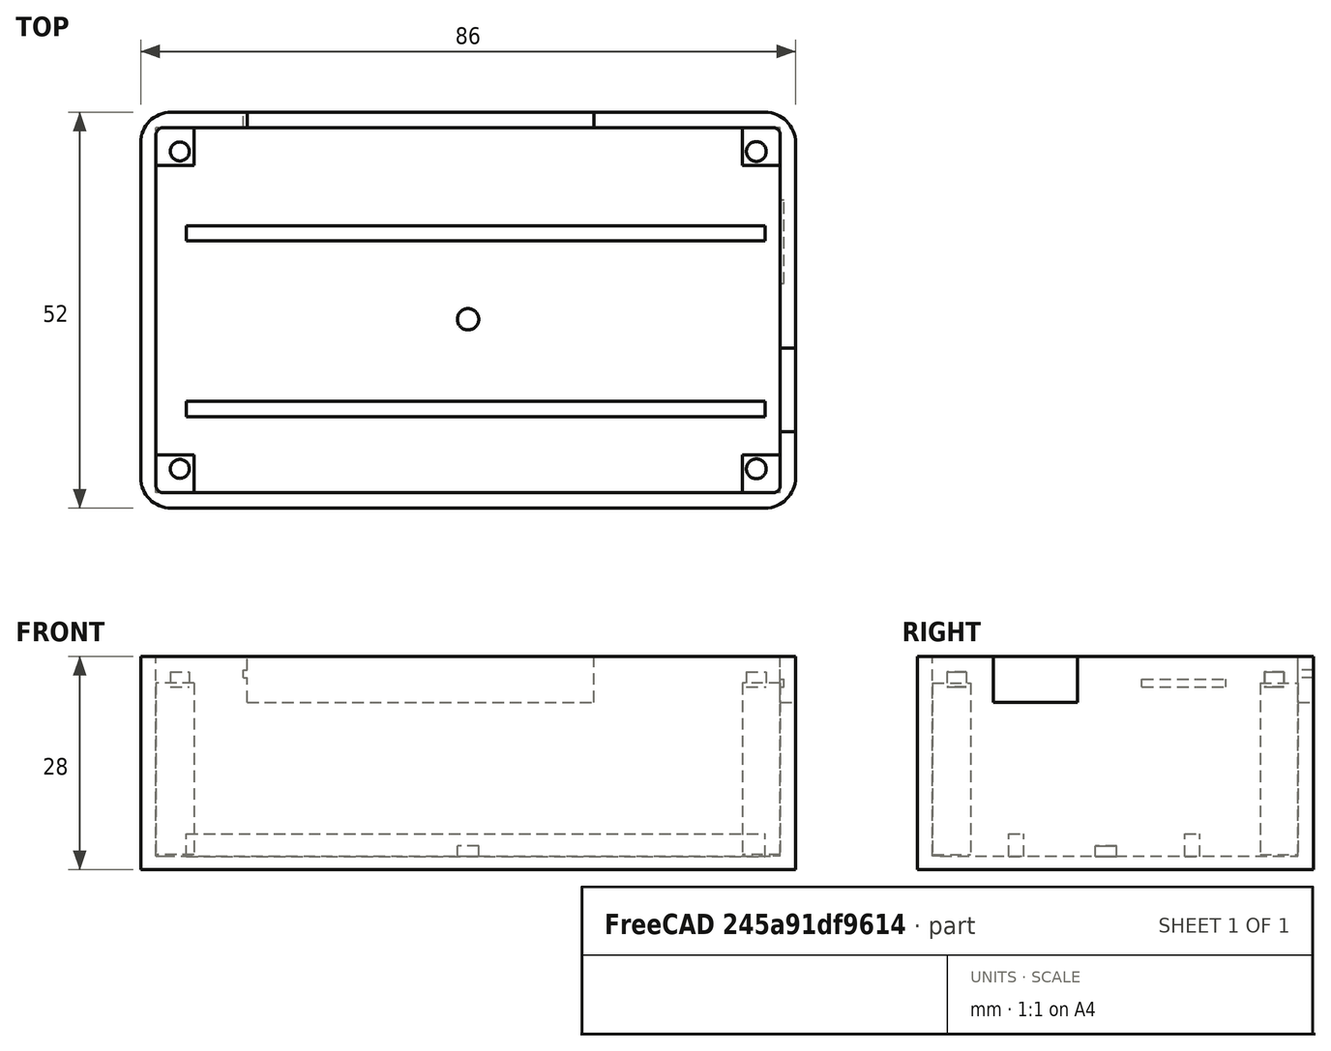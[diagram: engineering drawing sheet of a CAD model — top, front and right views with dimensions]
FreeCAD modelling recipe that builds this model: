
FCSTD DOCUMENT  (FreeCAD 0.18R4 (GitTag))
Label: T5s Case V6
License: All rights reserved
LicenseURL: http://en.wikipedia.org/wiki/All_rights_reserved
objects: Part::Box×12, Part::Cylinder×5, Part::Cut×4, App::DocumentObjectGroup×2, Part::Fillet×2, Part::Fuse×1
note: 24 computed .brp shape members not serialized (recipe doc carries the construction recipe); baked Part::Feature solids carry a one-line shape summary decoded from their .brp

FEATURE [Part::Box] Box004  label="Column1"
  AttacherType = Attacher::AttachEngine3D
  Height = 22.5
  Length = 5
  Placement = pos=(-36,19,9.5) rot=(0,1,0;3.14159rad)
  Width = 5
FEATURE [Part::Cylinder] Cylinder  label="Column Cylinder 1"
  Angle = 360
  AttacherType = Attacher::AttachEngine3D
  Height = 2
  Placement = pos=(-37.85,20.85,11) rot=(0,1,0;3.14159rad)
  Radius = 1.25
FEATURE [Part::Box] Box006  label="Column3"
  AttacherType = Attacher::AttachEngine3D
  Height = 22.5
  Length = 5
  Placement = pos=(-36,-24,9.5) rot=(0,1,0;3.14159rad)
  Width = 5
FEATURE [Part::Box] Box005  label="Column2"
  AttacherType = Attacher::AttachEngine3D
  Height = 22.5
  Length = 5
  Placement = pos=(41,19,9.5) rot=(0,1,0;3.14159rad)
  Width = 5
FEATURE [Part::Cylinder] Cylinder001  label="Column Cylinder 3"
  Angle = 360
  AttacherType = Attacher::AttachEngine3D
  Height = 2
  Placement = pos=(-37.85,-20.85,11) rot=(0,1,0;3.14159rad)
  Radius = 1.25
FEATURE [Part::Box] Box007  label="Column4"
  AttacherType = Attacher::AttachEngine3D
  Height = 22.5
  Length = 5
  Placement = pos=(41,-24,9.5) rot=(0,1,0;3.14159rad)
  Width = 5
FEATURE [Part::Cylinder] Cylinder002  label="Column Cylinder 2"
  Angle = 360
  AttacherType = Attacher::AttachEngine3D
  Height = 2
  Placement = pos=(37.85,20.85,11) rot=(0,1,0;3.14159rad)
  Radius = 1.3
FEATURE [Part::Cylinder] Cylinder003  label="Column Cylinder 4"
  Angle = 360
  AttacherType = Attacher::AttachEngine3D
  Height = 2
  Placement = pos=(37.85,-20.85,11) rot=(0,1,0;3.14159rad)
  Radius = 1.3
FEATURE [App::DocumentObjectGroup] Gruppe  label="Stands"
  Group = -> [Box004,Cylinder,Box006,Box005,Cylinder001,Box007,Cylinder002,Cylinder003]
FEATURE [Part::Box] Box018  label="Würfel008"
  AttacherType = Attacher::AttachEngine3D
  Height = 28
  Length = 82
  Placement = pos=(-41,-24,-15) rot=(0,0,1;0rad)
  Width = 48
FEATURE [Part::Fillet] Fillet010
  Base = -> Box018
  Edges = 4 edges r=1: [Edge1,Edge3,Edge5,Edge7]
  Placement = pos=(0,0,1.8) rot=(0,0,1;0rad)
FEATURE [Part::Box] Box017  label="Würfel007"
  AttacherType = Attacher::AttachEngine3D
  Height = 28
  Length = 86
  Placement = pos=(-43,-26,-15) rot=(0,0,1;0rad)
  Width = 52
FEATURE [Part::Fillet] Fillet009
  Base = -> Box017
  Edges = 4 edges r=4: [Edge1,Edge3,Edge5,Edge7]
FEATURE [Part::Cut] Cut011
  Base = -> Fillet009
  Tool = -> Fillet010
FEATURE [Part::Box] Box014  label="ButtonCut001"
  AttacherType = Attacher::AttachEngine3D
  Height = 6
  Length = 45.5
  Placement = pos=(-29,24,7) rot=(0,0,1;0rad)
  Width = 2
FEATURE [Part::Cylinder] Cylinder004  label="Zylinder"
  Angle = 360
  AttacherType = Attacher::AttachEngine3D
  Height = 1.4
  Placement = pos=(0,-1.2,-13.3) rot=(0,0,1;0rad)
  Radius = 1.4
FEATURE [Part::Box] Box021  label="Würfel010"
  AttacherType = Attacher::AttachEngine3D
  Height = 3
  Length = 76
  Placement = pos=(-37,9.1,-13.3) rot=(0,0,1;0rad)
  Width = 2
FEATURE [Part::Box] Box020  label="Würfel009"
  AttacherType = Attacher::AttachEngine3D
  Height = 3
  Length = 76
  Placement = pos=(-37,-14,-13.3) rot=(0,0,1;0rad)
  Width = 2
FEATURE [App::DocumentObjectGroup] Gruppe001  label="Battery"
  Group = -> [Box020,Box021,Cylinder004]
FEATURE [Part::Box] Box019  label="LidHolder"
  AttacherType = Attacher::AttachEngine3D
  Height = 1
  Length = 1
  Placement = pos=(-29.5,24,10.2) rot=(0,0,1;0rad)
  Width = 2
FEATURE [Part::Fuse] Fusion
  Base = -> Box014
  Tool = -> Box019
FEATURE [Part::Box] Box015  label="USB Cut001"
  AttacherType = Attacher::AttachEngine3D
  Height = 6
  Length = 2
  Placement = pos=(41,-16,7) rot=(0,0,1;0rad)
  Width = 11
FEATURE [Part::Box] Box016  label="Cliphole001"
  AttacherType = Attacher::AttachEngine3D
  Height = 1
  Length = 0.5
  Placement = pos=(41,3.5,9) rot=(0,0,1;0rad)
  Width = 11
FEATURE [Part::Cut] Cut
  Base = -> Cut011
  Tool = -> Fusion
FEATURE [Part::Cut] Cut012
  Base = -> Cut
  Tool = -> Box015
FEATURE [Part::Cut] Cut013
  Base = -> Cut012
  Tool = -> Box016
